# Revit family: Deca_Cuba de sobrepor redonda_Cubas sobrepor_L.1050
name_source: partatom
category: Plumbing Fixtures
units: mm (PartAtom-declared; Revit-internal decimal feet)

## family parameters
Cut with Voids When Loaded = Yes
Host = Face
Part Type = Normal
Room Calculation Point = No
Round Connector Dimension = Use Radius
Shared = No

## types (17) — shared parameters
Acompanha o Produto = -
Aprovado por = quattroD
Atendimento ao Cliente = 0800-0117073
Categoria = CUBAS
Composição Anel Vedação = -
Composição Assento = -
Composição Básica = Argila, feldspato, caulim, vidrados e corantes inorgânicos.
Composição Componente = Não Possui
Consumo = -
Cor Secundária = -
Criado por = quattroD
Código Pai = L.1050
Description = Cuba de sobrepor redonda
Diâmetro Ponto de Esgoto = 25 mm  [stored 0.082021 ft]
Informações Complementares = -
Itens de Instalação = 1601.C; 1601.C.CLI; 1602.C; 1602.C.PLA; 1680.C.100.112; 1682.C.100.112; 1684.C.100.112
Linha = Cubas Sobrepor
Manufacturer = Deca
Norma = NBR-16728-1;NBR-16728-2
Pressão máx. funcionamento = -
Pressão mín. Aquec. Acúmulo = -
Pressão mín. Aquec. Passagem = -
Pressão mín. funcionamento = -
Raio Ponto de Esgoto = 13 mm  [stored 0.0426509 ft]
Saída de Esgoto = Válvula Curta
Segmento = Banheiro Luxo
Tipo de dispositivo economizador = -
Tipo de mecanismo utilizado = -
Tipo de rosca de entrada = -
Tipo de rosca de saída = -
URL = www.deca.com.br
Vazão na Pressão máx. (L/min) = -
Vazão na Pressão mín. (L/min) = -
zero-valued in all types: Default Elevation

## per-type parameters (varying)
| type | Cor Interna | Cor Principal | Cores Componente | Material | Material Secundário | Model | Peso Líquido (Kg) |
| L.1050.17_Branco | - | Branco | Não Possui | Deca_Branco | <By Category> | L.1050.17 | 7.115 |
| L.1050.94_Ébano Fosco | - | Ébano fosco | Não Possui | Deca_Ébano Fosco | <By Category> | L.1050.94 | 7.115 |
| L.1050.95_Ébano | - | Ébano | Não Possui | Deca_Ébano | Deca_Ébano | L.1050.95 | 7.115 |
| L.1050.22_Marrom Fosco | - | Marrom fosco | Não Possui | Deca_Marrom Fosco | <By Category> | L.1050.22 | 7.115 |
| L.1050.04_Prata | - | Prata | Não Possui | Deca_Prata | <By Category> | L.1050.04 | 11.662 |
| L.1050.86_Cinza Fosco | - | Cinza fosco | Não Possui | Deca_Cinza Fosco | <By Category> | L.1050.86 | 7.115 |
| L.1050.03_Dourado | - | Dourado | Não Possui | Deca_Dourado | <By Category> | L.1050.03 | 11.662 |
| L.1050.16_Branco Fosco | - | Branco fosco | Não Possui | Deca_Branco Fosco | <By Category> | L.1050.16 | 7.115 |
| L.1050.21_Marfim - Marfim | - | Marfim | Não Possui | Deca_Marfim | Deca_Marfim | L.1050.21 | 7.115 |
| L.1050.71_Kale Green - Branco Fosco | 16 - Branco Fosco | Kale green | - | Deca_Kale Green | Deca_Branco Fosco | L.1050.71 | 7.115 |
| L.1050.72_Ébano Fosco - Branco Fosco | 16 - Branco Fosco | Ébano fosco | - | Deca_Ébano Fosco | Deca_Branco Fosco | L.1050.72 | 7.115 |
| L.1050.73_Marrom Fosco - Branco Fosco | 16 - Branco Fosco | Marrom fosco | - | Deca_Marrom Fosco | Deca_Branco Fosco | L.1050.73 | 7.115 |
| L.1050.30_Cacao | - | Cacao | Não Possui | Deca_Cacao | <By Category> | L.1050.30 | 7.115 |
| L.1050.31_Caramelo Fosco | - | Caramelo fosco | Não Possui | Deca_Caramelo Fosco | <By Category> | L.1050.31 | 7.115 |
| L.1050.42_Kale Green | - | Kale green | Não Possui | Deca_Kale Green | <By Category> | L.1050.42 | 0.748 |
| L.1050.47_Menta | - | Menta | Não Possui | Deca_Menta | <By Category> | L.1050.47 | 7.115 |
| L.1050.48_Pistache | - | Pistache | Não Possui | Deca_Pistache | <By Category> | L.1050.48 | 10.132 |

note: [stored X ft] marks values corroborated as IEEE doubles in the binary element streams (Revit-internal decimal feet)

## geometry (parser evidence)
native form markers: Sweep x1
no freeform markers — native parametric forms only
